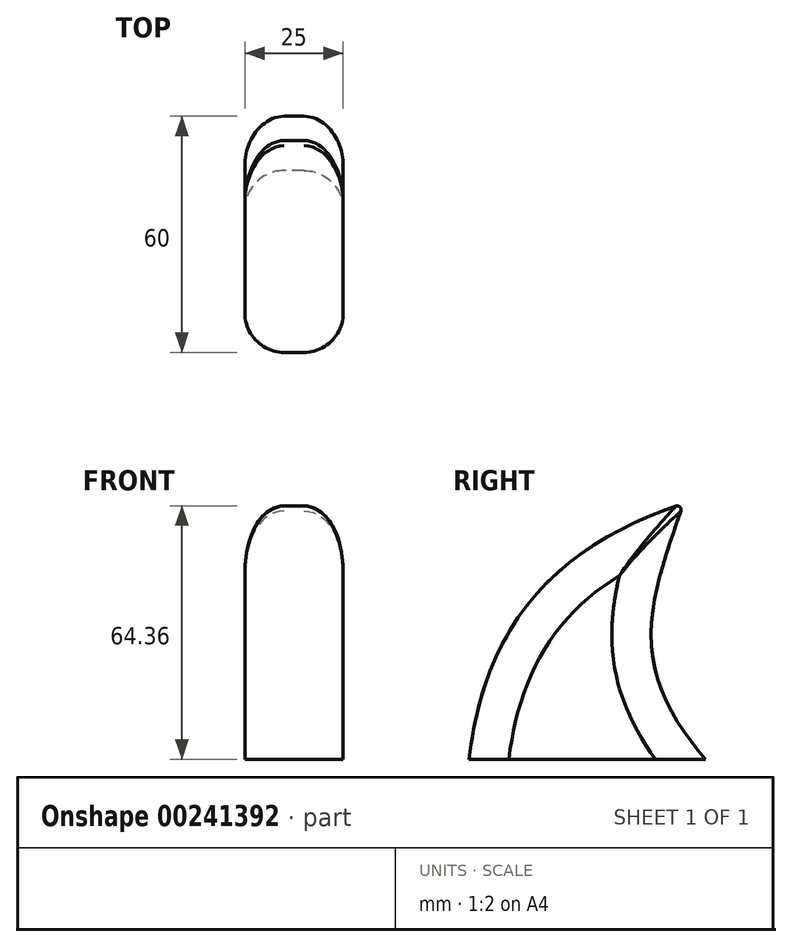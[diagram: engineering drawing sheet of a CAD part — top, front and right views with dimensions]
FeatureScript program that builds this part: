
annotation { "Feature Type Name" : "Feature", "Feature Type Description" : "" }
export const myFeature = defineFeature(function(context is Context, id is Id, definition is map)
    precondition{}
    {
        {
            var Q0;
            Q0=qCreatedBy(makeId("Right.planeOp"),FACE);
            var sketch = newSketch(context, id + "F0", { "sketchPlane" : qUnion([Q0])});
            skLineSegment(sketch, "E0", {"start": v(-40, 0) * mm, "end": v(20, 0) * mm});
            skPoint(sketch, "E1", {"position": v(14.45, 64.96) * mm});
            skFitSpline(sketch, "E2", {"points": [v(-40, 0) * mm, v(14.45, 64.96) * mm], "startDerivative": vector(11.33, 99.26) * mm, "endDerivative": vector(101.04, 33.38) * mm});
            skFitSpline(sketch, "E3", {"points": [v(20, 0) * mm, v(14.45, 64.96) * mm], "startDerivative": vector(-60, 70.4) * mm, "endDerivative": vector(27.97, 79.4) * mm});
            skSolve(sketch);
        }
        {
            var Q0;
            Q0 = qSketchRegion(id + "F0", true);
            extrude(context, id + "F1", {"entities" : qUnion([Q0]), "depth" : 25 * mm});
        }
        {
            var Q0;
            Q0=makeQuery(id+"F1.opExtrude","CAP_EDGE",EDGE,{"disambiguationData":[OSD([sQuery(id+"F0.wireOp",EDGE,"E2")])],"isStart":true});
            var Q1;
            Q1=makeQuery(id+"F1.opExtrude","CAP_EDGE",EDGE,{"disambiguationData":[OSD([sQuery(id+"F0.wireOp",EDGE,"E2")])],"isStart":false});
            var Q2;
            Q2=makeQuery(id+"F1.opExtrude","CAP_EDGE",EDGE,{"disambiguationData":[OSD([sQuery(id+"F0.wireOp",EDGE,"E3")])],"isStart":false});
            var Q3;
            Q3=makeQuery(id+"F1.opExtrude","CAP_EDGE",EDGE,{"disambiguationData":[OSD([sQuery(id+"F0.wireOp",EDGE,"E3")])],"isStart":true});
            fillet(context, id + "F2", {"entities" : qUnion([Q0, Q1, Q2, Q3]), "radius" : 10 * mm, "tangentPropagation" : true, "allowEdgeOverflow" : false});
        }
        {
            var Q0;
            Q0=makeQuery(id+"F1.opExtrude","SWEPT_EDGE",EDGE,{"disambiguationData":[OSD([sQuery(id+"F0.wireOp",EDGE,"E2"),sQuery(id+"F0.wireOp",EDGE,"E3")])]});
            fillet(context, id + "F3", {"entities" : qUnion([Q0]), "radius" : 1 * mm, "tangentPropagation" : true, "allowEdgeOverflow" : false});
        }
    });
